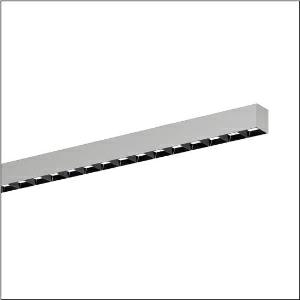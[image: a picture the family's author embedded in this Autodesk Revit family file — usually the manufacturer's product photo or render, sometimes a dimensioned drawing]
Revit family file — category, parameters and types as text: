
# Revit family: silica_r__21_51mx22tctas_2eab
name_source: partatom
category: Lighting Fixtures
units: mm (PartAtom-declared; Revit-internal decimal feet)

## family parameters
Cut with Voids When Loaded = No
Host = Face
Light Source = No
Part Type = Normal
Room Calculation Point = No
Round Connector Dimension = Use Diameter
Shared = No

## types (1)
- --- (1 x LED, 9300 lm, 80.4 W, 6500K)
    Apparent Load = 80 VA
    CIE Flux Codes = 84 100 100 100 100
    Color Rendering = 80
    Color Temperature = 6500K
    Default Elevation = 1800 mm
    Description = Silica® 21, office luminaire, primary light control with darklight reflector, of PMMA, black, CAT 2 (L<= 3000cd/m²), light emission: direct distribution, primary light characteristic: symmetric, installation type: surface-mounted, LED, rated luminous flux: 9.300lm, luminous efficacy: 110lm/W, light colour: 8tw, colour temperature: 2700..6500K, control gear: ECG DALI, with terminal, 3+2-pole, max. 2.5mm², mains connection: 220..240V, AC, 50/60Hz, rated input power: 84.5W, luminaire housing, of aluminium, metallic grey (RAL 9006), length: 3.004mm, width: 53mm, height: 53mm, protection rating (complete): IP20, insulation class (complete): insulation class I (protective earthing), certification: CE, permissible operating ambient temperature: 0..+35°C, standard: EN 50419, packaging unit: 1 piece
    Height = 0 mm  [stored 0 ft]
    Lamp = 1 x LED
    Lamp Light Flux = 9300 lm
    Lamp Power = 80.4 W
    Lamp count = 1
    Length = 3004 mm
    Luminous efficacy = 116 lm/W
    Manufacturer = Siteco
    ModVariant = No
    Model = 51MX22TCTAS
    Mounting Place = Ceiling
    Mounting Type = Recessed
    Number of Poles = 1
    OnlyDefault = Yes
    Power Factor = 1
    Product Name = Silica® 21
    Product group = office luminaire | ceiling recessed
    ProductGroupID = 401
    Protection Class = Protection class I
    Protection Degree = IP 20
    RLX_Detail_Level = 1
    RLX_Emergency_Light_Flux = 0 lm
    RLX_Emergency_Type = 0
    RLX_Emergency_Type_DB = No
    RlxData = <blob elided: 60125 chars, md5=3ab2301c>
    Socket = socket
    Standby Power = 0 W
    System Light Flux = 9300 lm
    System Power = 80 W
    Type Comments = individual setting
    Type Image = l_1313585.jpg
    URL = http://relux.com
    VarID = @adj_089481
    Voltage = 0 V
    Weight = 0.00 kg
    Width = 53 mm

note: [stored X ft] marks values corroborated as IEEE doubles in the binary element streams (Revit-internal decimal feet)

## geometry (parser evidence)
native form markers: Blend x4, Sweep x11
no freeform markers — native parametric forms only
